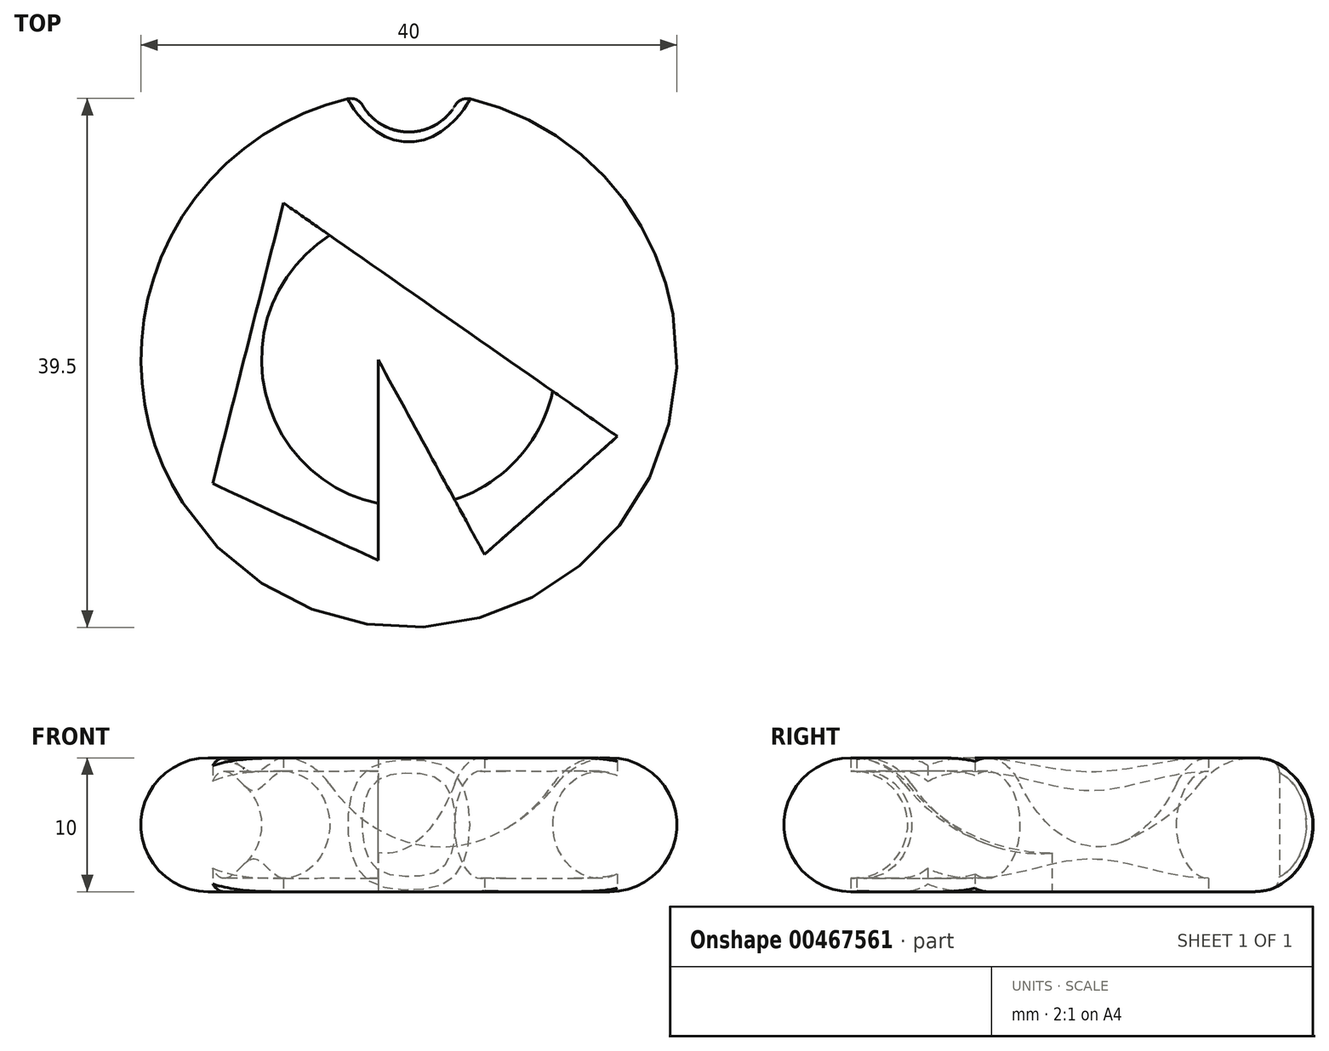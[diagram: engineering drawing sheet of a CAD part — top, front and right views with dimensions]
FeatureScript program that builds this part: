
annotation { "Feature Type Name" : "Feature", "Feature Type Description" : "" }
export const myFeature = defineFeature(function(context is Context, id is Id, definition is map)
    precondition{}
    {
        {
            var Q0;
            Q0=qCreatedBy(makeId("Front.planeOp"),FACE);
            var sketch = newSketch(context, id + "F0", { "sketchPlane" : qUnion([Q0])});
            skArc(sketch, "E0", {"start": v(-11.07, 8.09) * mm, "mid": v(-6.15, 4.12) * mm, "end": v(0, 2.7) * mm});
            skArc(sketch, "E1", {"start": v(-11.07, 8.09) * mm, "mid": v(-19.5, 7.19) * mm, "end": v(-15, 0) * mm});
            skLineSegment(sketch, "E2", {"start": v(-15, 0) * mm, "end": v(0, 0) * mm});
            skLineSegment(sketch, "E3", {"start": v(0, 0) * mm, "end": v(0, 2.7) * mm});
            skSolve(sketch);
        }
        {
            var Q0;
            Q0 = qSketchRegion(id + "F0", true);
            var Q1;
            Q1=sQuery(id+"F0.wireOp",EDGE,"E3");
            revolve(context, id + "F1", {"entities" : qUnion([Q0]), "axis" : qUnion([Q1]), "revolveType" : RevolveType.FULL});
        }
        {
            var Q0;
            Q0=qCreatedBy(makeId("Top.planeOp"),FACE);
            var sketch = newSketch(context, id + "F2", { "sketchPlane" : qUnion([Q0])});
            skLineSegment(sketch, "E4", {"start": v(15.57, -5.74) * mm, "end": v(-9.36, 11.7) * mm});
            skLineSegment(sketch, "E5", {"start": v(-9.36, 11.7) * mm, "end": v(-14.65, -9.27) * mm});
            skLineSegment(sketch, "E6", {"start": v(-14.65, -9.27) * mm, "end": v(-2.3, -15) * mm});
            skLineSegment(sketch, "E7", {"start": v(-2.3, -15) * mm, "end": v(-2.3, 0) * mm});
            skLineSegment(sketch, "E8", {"start": v(-2.3, 0) * mm, "end": v(5.64, -14.56) * mm});
            skLineSegment(sketch, "E9", {"start": v(5.64, -14.56) * mm, "end": v(15.57, -5.74) * mm});
            skSolve(sketch);
        }
        {
            var Q0;
            Q0=makeQuery(id+"F2.imprint","IMPRINT",FACE,{"disambiguationData":[TD([[makeQuery(id+"F2.imprint","IMPRINT",EDGE,{"derivedFrom":sQuery(id+"F2.wireOp",EDGE,"E4")}),1.0]])]});
            extrude(context, id + "F3", {"entities" : qUnion([Q0]), "operationType" : NewBodyOperationType.REMOVE, "endBound" : BoundingType.THROUGH_ALL, "depth" : 25 * mm});
        }
        {
            var Q0;
            Q0=qCreatedBy(makeId("Front.planeOp"),FACE);
            var sketch = newSketch(context, id + "F4", { "sketchPlane" : qUnion([Q0])});
            skCircle(sketch, "E10", {"center": v(-15, 5) * mm, "radius": 4 * mm});
            skSolve(sketch);
        }
        {
            var Q0;
            Q0 = qSketchRegion(id + "F4", true);
            var Q1;
            Q1=sQuery(id+"F0.wireOp",EDGE,"E3");
            revolve(context, id + "F5", {"operationType" : NewBodyOperationType.ADD, "entities" : qUnion([Q0]), "axis" : qUnion([Q1]), "revolveType" : RevolveType.FULL});
        }
        {
            var Q0;
            Q0=qCreatedBy(makeId("Top.planeOp"),FACE);
            var sketch = newSketch(context, id + "F6", { "sketchPlane" : qUnion([Q0])});
            skCircle(sketch, "E11", {"center": v(0, 21) * mm, "radius": 4 * mm});
            skSolve(sketch);
        }
        {
            var Q0;
            Q0 = qSketchRegion(id + "F6", true);
            extrude(context, id + "F7", {"entities" : qUnion([Q0]), "operationType" : NewBodyOperationType.REMOVE, "endBound" : BoundingType.THROUGH_ALL, "depth" : 25 * mm});
        }
        {
            var Q0;
            Q0=makeQuery(id+"F7.boolean.opBoolean","INTERSECT",EDGE,{"derivedFrom":[makeQuery(id+"F1.opRevolve","SWEPT_FACE",FACE,{"disambiguationData":[OSD([sQuery(id+"F0.wireOp",EDGE,"E1")])]}),makeQuery(id+"F7.opExtrude","SWEPT_FACE",FACE,{"disambiguationData":[OSD([sQuery(id+"F6.wireOp",EDGE,"E11")])]})]});
            fillet(context, id + "F8", {"entities" : qUnion([Q0]), "radius" : 1 * mm, "tangentPropagation" : true, "allowEdgeOverflow" : false});
        }
    });
